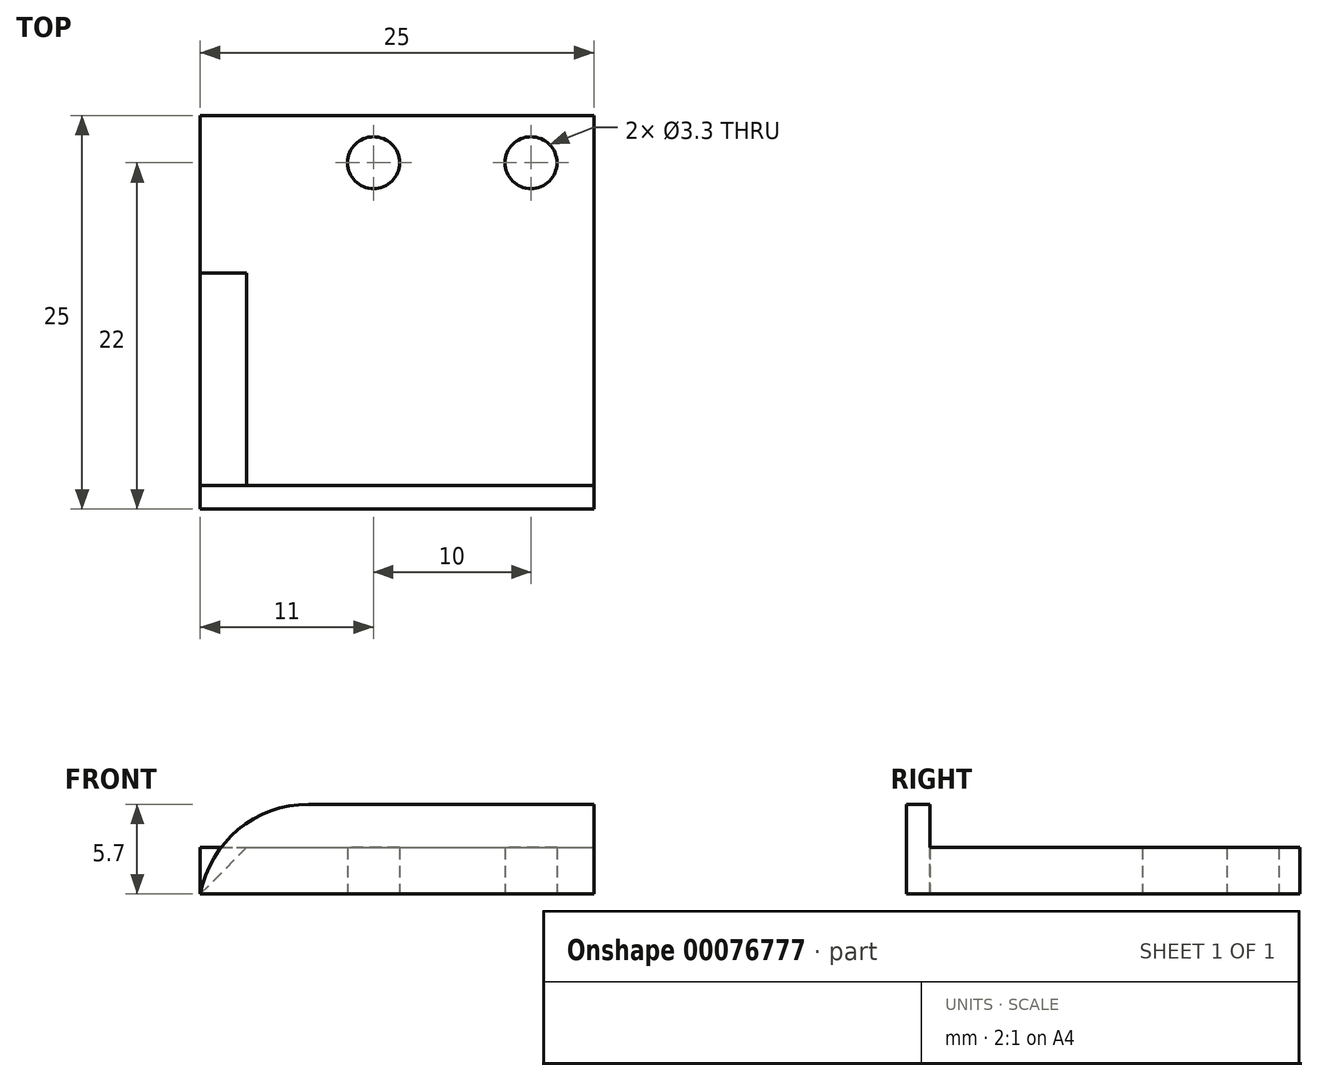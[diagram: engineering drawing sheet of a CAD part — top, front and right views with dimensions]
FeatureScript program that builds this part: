
annotation { "Feature Type Name" : "Feature", "Feature Type Description" : "" }
export const myFeature = defineFeature(function(context is Context, id is Id, definition is map)
    precondition{}
    {
        {
            var Q0;
            Q0=qCreatedBy(makeId("Top.planeOp"),FACE);
            var sketch = newSketch(context, id + "F0", { "sketchPlane" : qUnion([Q0])});
            skLineSegment(sketch, "E0.bottom", {"start": v(-12.5, 25) * mm, "end": v(12.5, 25) * mm});
            skLineSegment(sketch, "E0.top", {"start": v(-12.5, 0) * mm, "end": v(12.5, 0) * mm});
            skLineSegment(sketch, "E0.left", {"start": v(-12.5, 25) * mm, "end": v(-12.5, 0) * mm});
            skLineSegment(sketch, "E0.right", {"start": v(12.5, 25) * mm, "end": v(12.5, 0) * mm});
            skLineSegment(sketch, "E1", {"start": v(0, 0) * mm, "end": v(0, 25) * mm});
            skSolve(sketch);
        }
        {
            var Q0;
            {var subQ0=sQuery(id+"F0.wireOp",EDGE,"E0.left");Q0=makeQuery(id+"F0.imprint","IMPRINT",FACE,{"disambiguationData":[TD([[makeQuery(id+"F0.imprint","IMPRINT",EDGE,{"derivedFrom":subQ0}),1.0]])]});}
            var Q1;
            {var subQ0=sQuery(id+"F0.wireOp",EDGE,"E0.right");Q1=makeQuery(id+"F0.imprint","IMPRINT",FACE,{"disambiguationData":[TD([[makeQuery(id+"F0.imprint","IMPRINT",EDGE,{"derivedFrom":subQ0}),-1.0]])]});}
            extrude(context, id + "F1", {"entities" : qUnion([Q0, Q1]), "depth" : (7.5 - 1.8) * mm});
        }
        {
            var Q0;
            Q0=makeQuery(id+"F1.opExtrude","SWEPT_FACE",FACE,{"disambiguationData":[OSD([sQuery(id+"F0.wireOp",EDGE,"E0.right")])]});
            var sketch = newSketch(context, id + "F2", { "sketchPlane" : qUnion([Q0])});
            skLineSegment(sketch, "E2.bottom", {"start": v(25, 5.7) * mm, "end": v(1.5, 5.7) * mm});
            skLineSegment(sketch, "E2.top", {"start": v(25, 2.95) * mm, "end": v(1.5, 2.95) * mm});
            skLineSegment(sketch, "E2.left", {"start": v(25, 5.7) * mm, "end": v(25, 2.95) * mm});
            skLineSegment(sketch, "E2.right", {"start": v(1.5, 5.7) * mm, "end": v(1.5, 2.95) * mm});
            skSolve(sketch);
        }
        {
            var Q0;
            Q0=makeQuery(id+"F2.imprint","IMPRINT",FACE,{"disambiguationData":[TD([[makeQuery(id+"F2.imprint","IMPRINT",EDGE,{"derivedFrom":sQuery(id+"F2.wireOp",EDGE,"E2.bottom")}),1.0]])]});
            extrude(context, id + "F3", {"entities" : qUnion([Q0]), "operationType" : NewBodyOperationType.REMOVE, "endBound" : BoundingType.THROUGH_ALL, "oppositeDirection" : true, "depth" : 25 * mm});
        }
        {
            var Q0;
            Q0=makeQuery(id+"F3.boolean.opBoolean","COPY",FACE,{"derivedFrom":makeQuery(id+"F3.opExtrude","SWEPT_FACE",FACE,{"disambiguationData":[OSD([sQuery(id+"F2.wireOp",EDGE,"E2.right")])]})});
            var sketch = newSketch(context, id + "F4", { "sketchPlane" : qUnion([Q0])});
            skLineSegment(sketch, "E3", {"start": v(12.5, 0) * mm, "end": v(9.55, 2.95) * mm});
            skLineSegment(sketch, "E4", {"start": v(9.55, 2.95) * mm, "end": v(12.5, 2.95) * mm});
            skLineSegment(sketch, "E5", {"start": v(12.5, 2.95) * mm, "end": v(12.5, 0) * mm});
            skSolve(sketch);
        }
        {
            var Q0;
            Q0=makeQuery(id+"F4.imprint","IMPRINT",FACE,{"disambiguationData":[TD([[makeQuery(id+"F4.imprint","IMPRINT",EDGE,{"derivedFrom":sQuery(id+"F4.wireOp",EDGE,"E3")}),-1.0]])]});
            var Q1;
            Q1=makeQuery(id+"F3.boolean.opBoolean","COPY",FACE,{"derivedFrom":makeQuery(id+"F3.opExtrude","SWEPT_FACE",FACE,{"disambiguationData":[OSD([sQuery(id+"F2.wireOp",EDGE,"E2.right")])]})});
            extrude(context, id + "F5", {"entities" : qUnion([Q0]), "operationType" : NewBodyOperationType.REMOVE, "endBoundEntityFace" : qUnion([Q1]), "depth" : 13.5 * mm});
        }
        {
            var Q0;
            Q0=makeQuery(id+"F1.opExtrude","CAP_EDGE",EDGE,{"disambiguationData":[OSD([sQuery(id+"F0.wireOp",EDGE,"E0.left")])],"isStart":false});
            fillet(context, id + "F6", {"entities" : qUnion([Q0]), "radius" : (7) * mm, "tangentPropagation" : true, "allowEdgeOverflow" : false});
        }
        {
            var Q0;
            Q0=makeQuery(id+"F1.opExtrude","CAP_FACE",FACE,{"disambiguationData":[OSD([sQuery(id+"F0.wireOp",EDGE,"E0.bottom"),sQuery(id+"F0.wireOp",EDGE,"E0.top"),sQuery(id+"F0.wireOp",EDGE,"E0.left"),sQuery(id+"F0.wireOp",EDGE,"E0.right")])],"isStart":true});
            var sketch = newSketch(context, id + "F7", { "sketchPlane" : qUnion([Q0])});
            skCircle(sketch, "E6", {"center": v(8.5, -22) * mm, "radius": 1.65 * mm});
            skCircle(sketch, "E7", {"center": v(-1.5, -22) * mm, "radius": 1.65 * mm});
            skSolve(sketch);
        }
        {
            var Q0;
            Q0=makeQuery(id+"F7.imprint","IMPRINT",FACE,{"disambiguationData":[TD([[makeQuery(id+"F7.imprint","IMPRINT",EDGE,{"derivedFrom":sQuery(id+"F7.wireOp",EDGE,"E7")}),1.0]])]});
            var Q1;
            Q1=makeQuery(id+"F7.imprint","IMPRINT",FACE,{"disambiguationData":[TD([[makeQuery(id+"F7.imprint","IMPRINT",EDGE,{"derivedFrom":sQuery(id+"F7.wireOp",EDGE,"E6")}),1.0]])]});
            extrude(context, id + "F8", {"entities" : qUnion([Q0, Q1]), "operationType" : NewBodyOperationType.REMOVE, "endBound" : BoundingType.THROUGH_ALL, "oppositeDirection" : true, "depth" : 25 * mm});
        }
    });
